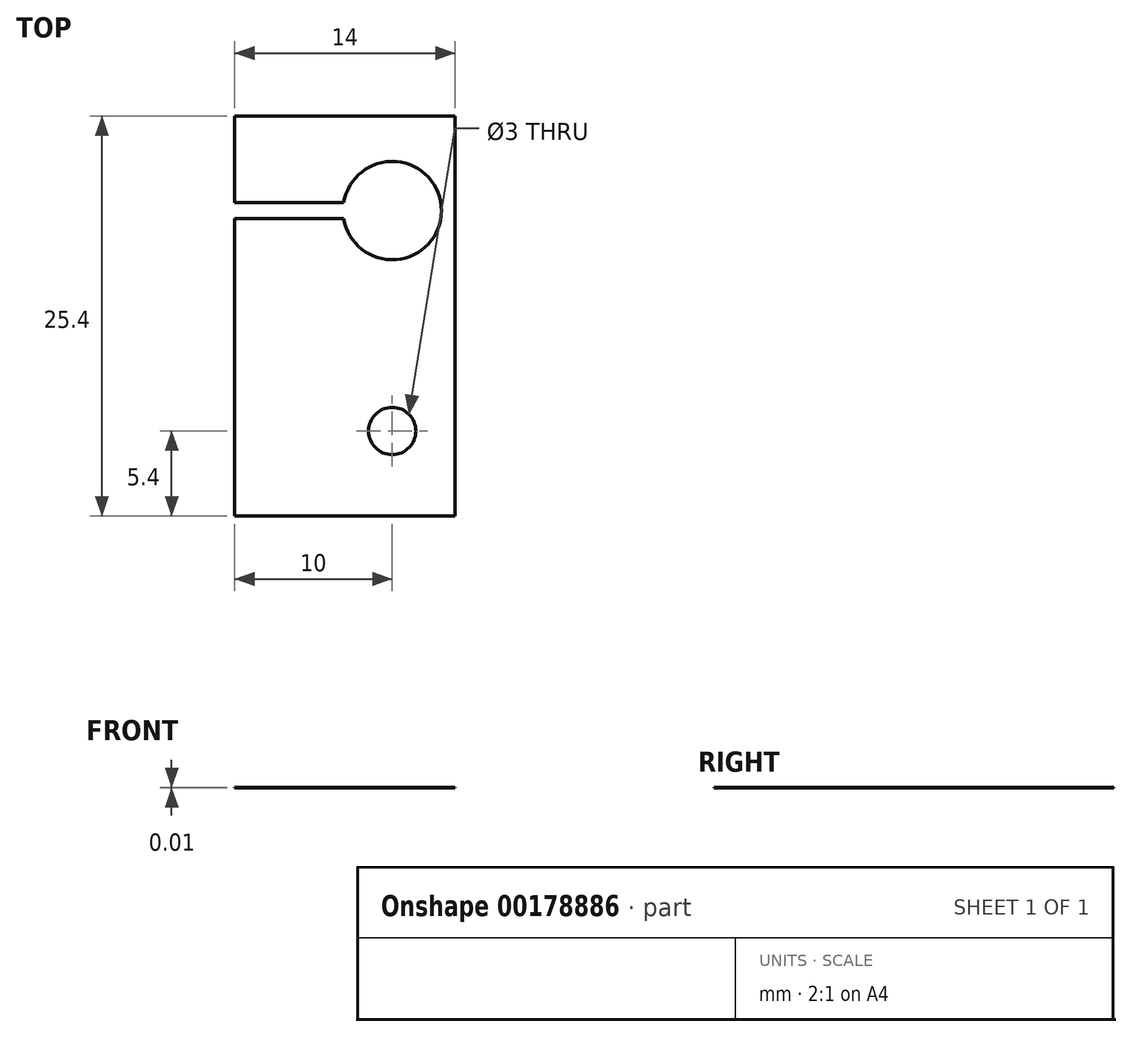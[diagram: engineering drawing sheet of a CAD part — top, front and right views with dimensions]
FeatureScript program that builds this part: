
annotation { "Feature Type Name" : "Feature", "Feature Type Description" : "" }
export const myFeature = defineFeature(function(context is Context, id is Id, definition is map)
    precondition{}
    {
        {
            var Q0;
            Q0=qCreatedBy(makeId("Top.planeOp"),FACE);
            var sketch = newSketch(context, id + "F0", { "sketchPlane" : qUnion([Q0])});
            skLineSegment(sketch, "E0.bottom", {"start": v(7, -12.7) * mm, "end": v(-7, -12.7) * mm});
            skLineSegment(sketch, "E0.top", {"start": v(7, 12.7) * mm, "end": v(-7, 12.7) * mm});
            skLineSegment(sketch, "E0.left", {"start": v(7, -12.7) * mm, "end": v(7, 12.7) * mm});
            skLineSegment(sketch, "E0.right", {"start": v(-7, -12.7) * mm, "end": v(-7, 6.2) * mm});
            skPoint(sketch, "E0.middle", {"position": v(0, 0) * mm});
            skArc(sketch, "E1", {"start": v(-0.08, 6.2) * mm, "mid": v(6.12, 6.7) * mm, "end": v(-0.08, 7.2) * mm});
            skCircle(sketch, "E2", {"center": v(3, -7.3) * mm, "radius": 1.5 * mm});
            skLineSegment(sketch, "E3.bottom", {"start": v(-4.5, 12.7) * mm, "end": v(-1.5, 12.7) * mm, "construction": true});
            skLineSegment(sketch, "E3.top", {"start": v(-4.5, -12.7) * mm, "end": v(-1.5, -12.7) * mm, "construction": true});
            skLineSegment(sketch, "E3.left", {"start": v(-4.5, 12.7) * mm, "end": v(-4.5, -12.7) * mm, "construction": true});
            skLineSegment(sketch, "E3.right", {"start": v(-1.5, 12.7) * mm, "end": v(-1.5, -12.7) * mm, "construction": true});
            skLineSegment(sketch, "E4.bottom", {"start": v(-7, 7.2) * mm, "end": v(-0.08, 7.2) * mm});
            skLineSegment(sketch, "E4.top", {"start": v(-7, 6.2) * mm, "end": v(-0.08, 6.2) * mm});
            skLineSegment(sketch, "E5.trimOffspring", {"start": v(-7, 7.2) * mm, "end": v(-7, 12.7) * mm});
            skSolve(sketch);
        }
        {
            var Q0;
            Q0=qSketchRegion(id+"F0",true);
            extrude(context, id + "F1", {"entities" : qUnion([Q0]), "depth" : 3 / 203.2 * mm});
        }
        {
            var Q0;
            Q0=makeQuery(id+"F1.opExtrude","SWEPT_FACE",FACE,{"disambiguationData":[OSD([sQuery(id+"F0.wireOp",EDGE,"E0.top")])]});
            var sketch = newSketch(context, id + "F2", { "sketchPlane" : qUnion([Q0])});
            skCircle(sketch, "E6", {"center": v(3.54, 4.76) * mm, "radius": 1.25 * mm});
            skLineSegment(sketch, "E7", {"start": v(7, 4.76) * mm, "end": v(0.08, 4.76) * mm, "construction": true});
            skSolve(sketch);
        }
        {
            var Q0;
            Q0=qSketchRegion(id+"F2",true);
            extrude(context, id + "F3", {"entities" : qUnion([Q0]), "operationType" : NewBodyOperationType.REMOVE, "endBound" : BoundingType.THROUGH_ALL, "oppositeDirection" : true, "depth" : 25 * mm});
        }
    });
